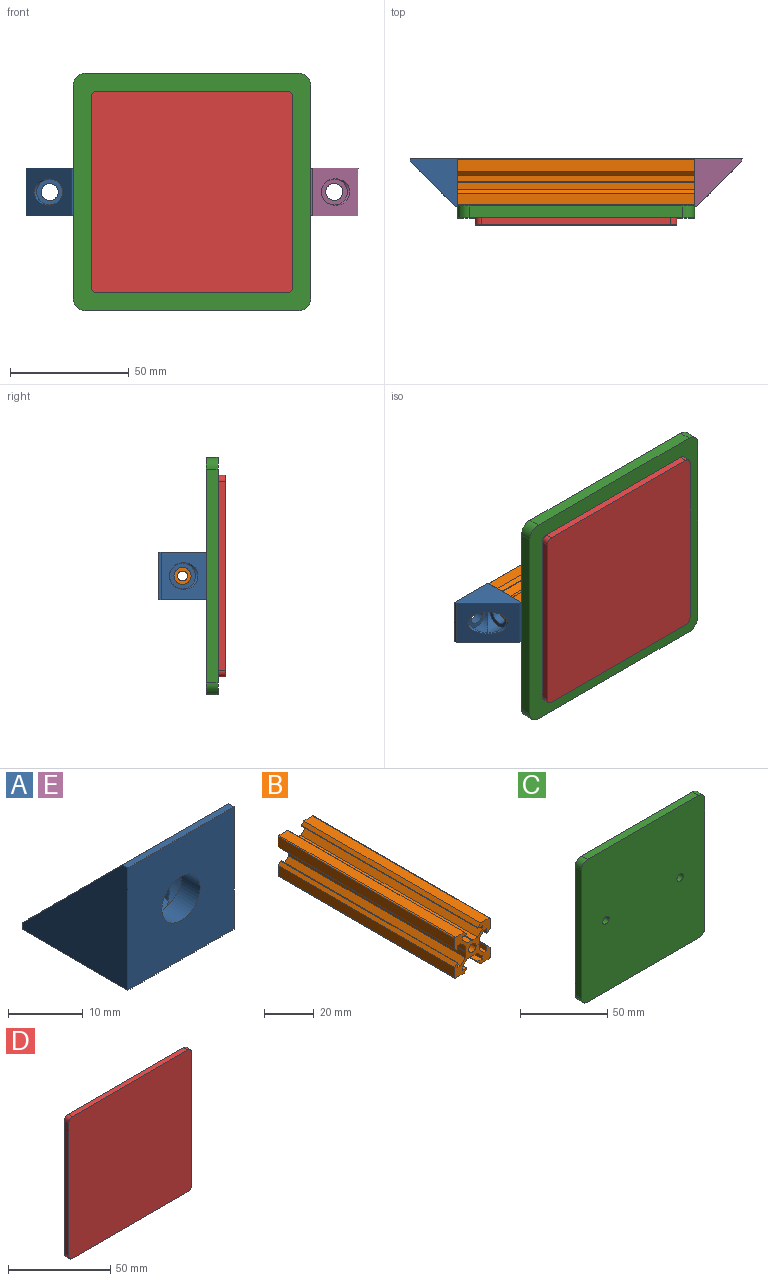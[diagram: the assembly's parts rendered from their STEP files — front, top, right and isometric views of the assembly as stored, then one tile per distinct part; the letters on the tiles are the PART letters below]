
ASSEMBLY  parts=5 mates=4
PART A: 15 faces, bbox 20x20x20 mm
  f0: cylinder r=5.5mm len=11mm, axis (0,0,1), area 17.8mm2, adj f12,f13,f14
  f1: cylinder r=3.6mm len=7.2mm, axis (0,1,0), area 79.2mm2, adj f6,f11
  f2: cylinder r=3.6mm len=7.2mm, axis (0,0,-1), area 79.2mm2, adj f4,f10
  f3: plane 20x1mm, normal (0,0,1), area 20mm2, adj f5,f6,f7,f14
  f4: plane 20x20mm, normal (0,0,-1), area 359.3mm2, adj f2,f5,f6,f7,f8
  f5: plane 20x20mm, normal (-1,0,0), area 219.5mm2, adj f3,f4,f6,f8,f14
  f6: plane 20x20mm, normal (0,-1,0), area 359.3mm2, adj f1,f3,f4,f5,f7
  f7: plane 20x20mm, normal (1,0,0), area 219.5mm2, adj f3,f4,f6,f8,f14
  f8: plane 20x1mm, normal (0,1,0), area 20mm2, adj f4,f5,f7,f14
  f9: cylinder r=5.5mm len=11mm, axis (0,0,1), area 103.6mm2, adj f10,f12,f13
  f10: plane 11x11mm, normal (0,0,1), area 54.3mm2, adj f2,f9
  f11: plane 11x11mm, normal (0,1,0), area 54.3mm2, adj f1,f12
  f12: cylinder r=5.5mm len=11mm, axis (0,1,0), area 103.6mm2, adj f0,f9,f11
  f13: cylinder r=5.5mm len=11mm, axis (0,1,0), area 17.8mm2, adj f0,f9,f14
  f14: plane 20x19mm, normal (0,0.71,0.71), area 387.5mm2, adj f0,f3,f5,f7,f8,f13
PART B: 71 faces, bbox 20x100x20 mm
  f0: plane 100x0.21mm, normal (0.71,0,0.71), area 29.7mm2, adj f1,f67,f69,f70
  f1: plane 100x0.21mm, normal (0.71,0,-0.71), area 29.7mm2, adj f0,f2,f69,f70
  f2: plane 100x2.63mm, normal (1,0,0), area 262.9mm2, adj f1,f3,f69,f70
  f3: plane 100x2.66mm, normal (0.71,0,-0.71), area 376.3mm2, adj f2,f4,f69,f70
  f4: plane 100x1.64mm, normal (0,0,-1), area 163.9mm2, adj f3,f5,f69,f70
  f5: plane 100x2.38mm, normal (-1,0,0), area 237.5mm2, adj f4,f6,f69,f70
  f6: plane 100x0.35mm, normal (0,0,-1), area 34.5mm2, adj f5,f7,f69,f70
  f7: plane 100x1.46mm, normal (0.71,0,-0.71), area 205.8mm2, adj f6,f8,f69,f70
  f8: plane 100x4.92mm, normal (1,0,0), area 492mm2, adj f7,f9,f69,f70
  f9: cylinder r=0.5mm len=100mm, axis (0,1,0), area 78.5mm2, adj f8,f10,f69,f70
  f10: plane 100x4.92mm, normal (0,0,1), area 492mm2, adj f9,f11,f69,f70
  f11: plane 100x1.46mm, normal (-0.71,0,0.71), area 205.8mm2, adj f10,f12,f69,f70
  f12: plane 100x0.35mm, normal (-1,0,0), area 34.5mm2, adj f11,f13,f69,f70
  f13: plane 100x2.38mm, normal (0,0,-1), area 237.5mm2, adj f12,f14,f69,f70
  f14: plane 100x1.64mm, normal (-1,0,0), area 163.9mm2, adj f13,f15,f69,f70
  f15: plane 100x2.66mm, normal (-0.71,0,0.71), area 376.3mm2, adj f14,f16,f69,f70
  f16: plane 100x2.63mm, normal (0,0,1), area 262.9mm2, adj f15,f17,f69,f70
  f17: plane 100x0.21mm, normal (-0.71,0,0.71), area 29.7mm2, adj f16,f18,f69,f70
  f18: plane 100x0.21mm, normal (0.71,0,0.71), area 29.7mm2, adj f17,f19,f69,f70
  f19: plane 100x2.63mm, normal (0,0,1), area 262.9mm2, adj f18,f20,f69,f70
  f20: plane 100x2.66mm, normal (0.71,0,0.71), area 376.3mm2, adj f19,f21,f69,f70
  f21: plane 100x1.64mm, normal (1,0,0), area 163.9mm2, adj f20,f22,f69,f70
  f22: plane 100x2.38mm, normal (0,0,-1), area 237.5mm2, adj f21,f23,f69,f70
  f23: plane 100x0.35mm, normal (1,0,0), area 34.5mm2, adj f22,f24,f69,f70
  f24: plane 100x1.46mm, normal (0.71,0,0.71), area 205.8mm2, adj f23,f25,f69,f70
  f25: plane 100x4.92mm, normal (0,0,1), area 492mm2, adj f24,f26,f69,f70
  f26: cylinder r=0.5mm len=100mm, axis (0,1,0), area 78.5mm2, adj f25,f27,f69,f70
  f27: plane 100x4.92mm, normal (-1,0,0), area 492mm2, adj f26,f28,f69,f70
  f28: plane 100x1.46mm, normal (-0.71,0,-0.71), area 205.8mm2, adj f27,f29,f69,f70
  f29: plane 100x0.35mm, normal (0,0,-1), area 34.5mm2, adj f28,f30,f69,f70
  f30: plane 100x2.38mm, normal (1,0,0), area 237.5mm2, adj f29,f31,f69,f70
  f31: plane 100x1.64mm, normal (0,0,-1), area 163.9mm2, adj f30,f32,f69,f70
  f32: plane 100x2.66mm, normal (-0.71,0,-0.71), area 376.3mm2, adj f31,f33,f69,f70
  f33: plane 100x2.63mm, normal (-1,0,0), area 262.9mm2, adj f32,f34,f69,f70
  f34: plane 100x0.21mm, normal (-0.71,0,-0.71), area 29.7mm2, adj f33,f35,f69,f70
  f35: plane 100x0.21mm, normal (-0.71,0,0.71), area 29.7mm2, adj f34,f36,f69,f70
  f36: plane 100x2.63mm, normal (-1,0,0), area 262.9mm2, adj f35,f37,f69,f70
  f37: plane 100x2.66mm, normal (-0.71,0,0.71), area 376.3mm2, adj f36,f38,f69,f70
  f38: plane 100x1.64mm, normal (0,0,1), area 163.9mm2, adj f37,f39,f69,f70
  f39: plane 100x2.38mm, normal (1,0,0), area 237.5mm2, adj f38,f40,f69,f70
  f40: plane 100x0.35mm, normal (0,0,1), area 34.5mm2, adj f39,f41,f69,f70
  f41: plane 100x1.46mm, normal (-0.71,0,0.71), area 205.8mm2, adj f40,f42,f69,f70
  f42: plane 100x4.92mm, normal (-1,0,0), area 492mm2, adj f41,f43,f69,f70
  f43: cylinder r=0.5mm len=100mm, axis (0,1,0), area 78.5mm2, adj f42,f44,f69,f70
  f44: plane 100x4.92mm, normal (0,0,-1), area 492mm2, adj f43,f45,f69,f70
  f45: plane 100x1.46mm, normal (0.71,0,-0.71), area 205.8mm2, adj f44,f46,f69,f70
  f46: plane 100x0.35mm, normal (1,0,0), area 34.5mm2, adj f45,f47,f69,f70
  f47: plane 100x2.38mm, normal (0,0,1), area 237.5mm2, adj f46,f48,f69,f70
  f48: plane 100x1.64mm, normal (1,0,0), area 163.9mm2, adj f47,f49,f69,f70
  f49: plane 100x2.66mm, normal (0.71,0,-0.71), area 376.3mm2, adj f48,f50,f69,f70
  f50: plane 100x2.63mm, normal (0,0,-1), area 262.9mm2, adj f49,f51,f69,f70
  f51: plane 100x0.21mm, normal (0.71,0,-0.71), area 29.7mm2, adj f50,f52,f69,f70
  f52: plane 100x0.21mm, normal (-0.71,0,-0.71), area 29.7mm2, adj f51,f53,f69,f70
  f53: plane 100x2.63mm, normal (0,0,-1), area 262.9mm2, adj f52,f54,f69,f70
  f54: plane 100x2.66mm, normal (-0.71,0,-0.71), area 376.3mm2, adj f53,f55,f69,f70
  f55: plane 100x1.64mm, normal (-1,0,0), area 163.9mm2, adj f54,f56,f69,f70
  f56: plane 100x2.38mm, normal (0,0,1), area 237.5mm2, adj f55,f57,f69,f70
  f57: plane 100x0.35mm, normal (-1,0,0), area 34.5mm2, adj f56,f58,f69,f70
  f58: plane 100x1.46mm, normal (-0.71,0,-0.71), area 205.8mm2, adj f57,f59,f69,f70
  f59: plane 100x4.92mm, normal (0,0,-1), area 492mm2, adj f58,f60,f69,f70
  f60: cylinder r=0.5mm len=100mm, axis (0,1,0), area 78.5mm2, adj f59,f61,f69,f70
  f61: plane 100x4.92mm, normal (1,0,0), area 492mm2, adj f60,f62,f69,f70
  f62: plane 100x1.46mm, normal (0.71,0,0.71), area 205.8mm2, adj f61,f63,f69,f70
  f63: plane 100x0.35mm, normal (0,0,1), area 34.5mm2, adj f62,f64,f69,f70
  f64: plane 100x2.38mm, normal (-1,0,0), area 237.5mm2, adj f63,f65,f69,f70
  f65: plane 100x1.64mm, normal (0,0,1), area 163.9mm2, adj f64,f66,f69,f70
  f66: plane 100x2.66mm, normal (0.71,0,0.71), area 376.3mm2, adj f65,f67,f69,f70
  f67: plane 100x2.63mm, normal (1,0,0), area 262.9mm2, adj f0,f66,f69,f70
  f68: cylinder r=2.1mm len=100mm, axis (0,1,0), area 1319.5mm2, adj f69,f70
  f69: plane 20x20mm, normal (0,-1,0), area 171.4mm2, adj f0,f1,f2,f3,f4,f5,f6,f7
  f70: plane 20x20mm, normal (0,1,0), area 171.4mm2, adj f0,f1,f2,f3,f4,f5,f6,f7
PART C: 12 faces, bbox 100x5x100 mm
  f0: cylinder r=5mm len=5mm, axis (0,1,0), area 39.3mm2, adj f1,f9,f10,f11
  f1: plane 90x5mm, normal (0,0,1), area 450mm2, adj f0,f2,f10,f11
  f2: cylinder r=5mm len=5mm, axis (0,1,0), area 39.3mm2, adj f1,f3,f10,f11
  f3: plane 90x5mm, normal (-1,0,0), area 450mm2, adj f2,f4,f10,f11
  f4: cylinder r=5mm len=5mm, axis (0,1,0), area 39.3mm2, adj f3,f5,f10,f11
  f5: plane 90x5mm, normal (0,0,-1), area 450mm2, adj f4,f6,f10,f11
  f6: cylinder r=5mm len=5mm, axis (0,1,0), area 39.3mm2, adj f5,f9,f10,f11
  f7: cylinder r=2.6mm len=5.2mm, axis (0,1,0), area 81.7mm2, adj f10,f11
  f8: cylinder r=2.6mm len=5.2mm, axis (0,1,0), area 81.7mm2, adj f10,f11
  f9: plane 90x5mm, normal (1,0,0), area 450mm2, adj f0,f6,f10,f11
  f10: plane 100x100mm, normal (0,-1,0), area 9936.1mm2, adj f0,f1,f2,f3,f4,f5,f6,f7
  f11: plane 100x100mm, normal (0,1,0), area 9936.1mm2, adj f0,f1,f2,f3,f4,f5,f6,f7
PART D: 10 faces, bbox 85x3x85 mm
  f0: cylinder r=2.5mm len=3mm, axis (0,1,0), area 11.8mm2, adj f1,f7,f8,f9
  f1: plane 80x3mm, normal (0,0,1), area 240mm2, adj f0,f2,f8,f9
  f2: cylinder r=2.5mm len=3mm, axis (0,1,0), area 11.8mm2, adj f1,f3,f8,f9
  f3: plane 80x3mm, normal (-1,0,0), area 240mm2, adj f2,f4,f8,f9
  f4: cylinder r=2.5mm len=3mm, axis (0,1,0), area 11.8mm2, adj f3,f5,f8,f9
  f5: plane 80x3mm, normal (0,0,-1), area 240mm2, adj f4,f6,f8,f9
  f6: cylinder r=2.5mm len=3mm, axis (0,1,0), area 11.8mm2, adj f5,f7,f8,f9
  f7: plane 80x3mm, normal (1,0,0), area 240mm2, adj f0,f6,f8,f9
  f8: plane 85x85mm, normal (0,-1,0), area 7219.6mm2, adj f0,f1,f2,f3,f4,f5,f6,f7
  f9: plane 85x85mm, normal (0,1,0), area 7219.6mm2, adj f0,f1,f2,f3,f4,f5,f6,f7
PART E: same geometry as A
PLACE A rot(axis=(-0.71,0,0.71),180deg) t=(-63.28,20.43,2.87)mm
PLACE B rot(axis=(0.58,0.58,-0.58),120deg) t=(446.72,20.43,2.87)mm
PLACE C rot(axis=(0.16,0.93,-0.34),0deg) t=(-3.28,10.43,2.87)mm
PLACE D rot(axis=(0.16,0.93,-0.34),0deg) t=(-3.28,5.43,2.87)mm
PLACE E rot(axis=(0.58,0.58,-0.58),120deg) t=(56.72,20.43,2.87)mm
MATE fastened D.f9 <-> C.f10  axis (0,1,0) through (-3.28,5.43,2.87)mm
MATE revolute E.f1 <-> B.f68  axis (-1,0,0) through (46.72,20.43,2.87)mm
MATE fastened B.f68 <-> C.f9  axis (1,0,0) through (46.72,20.43,2.87)mm
MATE revolute A.f0 <-> B.f68  axis (1,0,0) through (-53.28,20.43,2.87)mm
